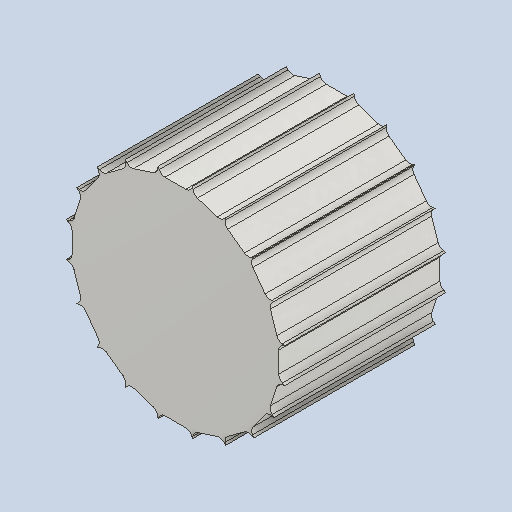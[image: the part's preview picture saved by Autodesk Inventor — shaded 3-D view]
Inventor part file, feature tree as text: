
AUTODESK INVENTOR PART (.ipt)
format: ipt  version: 2024 (Build 280153000, 153)  size: 238,592 bytes
history: native  units: mm (DEFAULTED — no unit token found)
features: other x3, extrude x2, fillet x1, pattern_circular x1
ambient origin geometry x8: Origin, YZ Plane, XZ Plane, XY Plane, X Axis, Y Axis, Z Axis, Center Point
bodies: Solid1 (feature_tree)
feature tree (7):
  other  "Pulley Sketch"
  extrude  "Base Body"  Depth=15.915494mm
  extrude  "Tooth"  Depth=0.3mm
  fillet  "Tooth Fillet"  Radius=1.25mm
  pattern_circular  "Teeth"  [2 undecoded]
  other  "Left flange"
  other  "Right flange"
note: 2 required parameter values undecoded (feature->parameter linkage not recoverable at this tier; creation-order binding heuristic only, values carry confidence <= 0.55)
